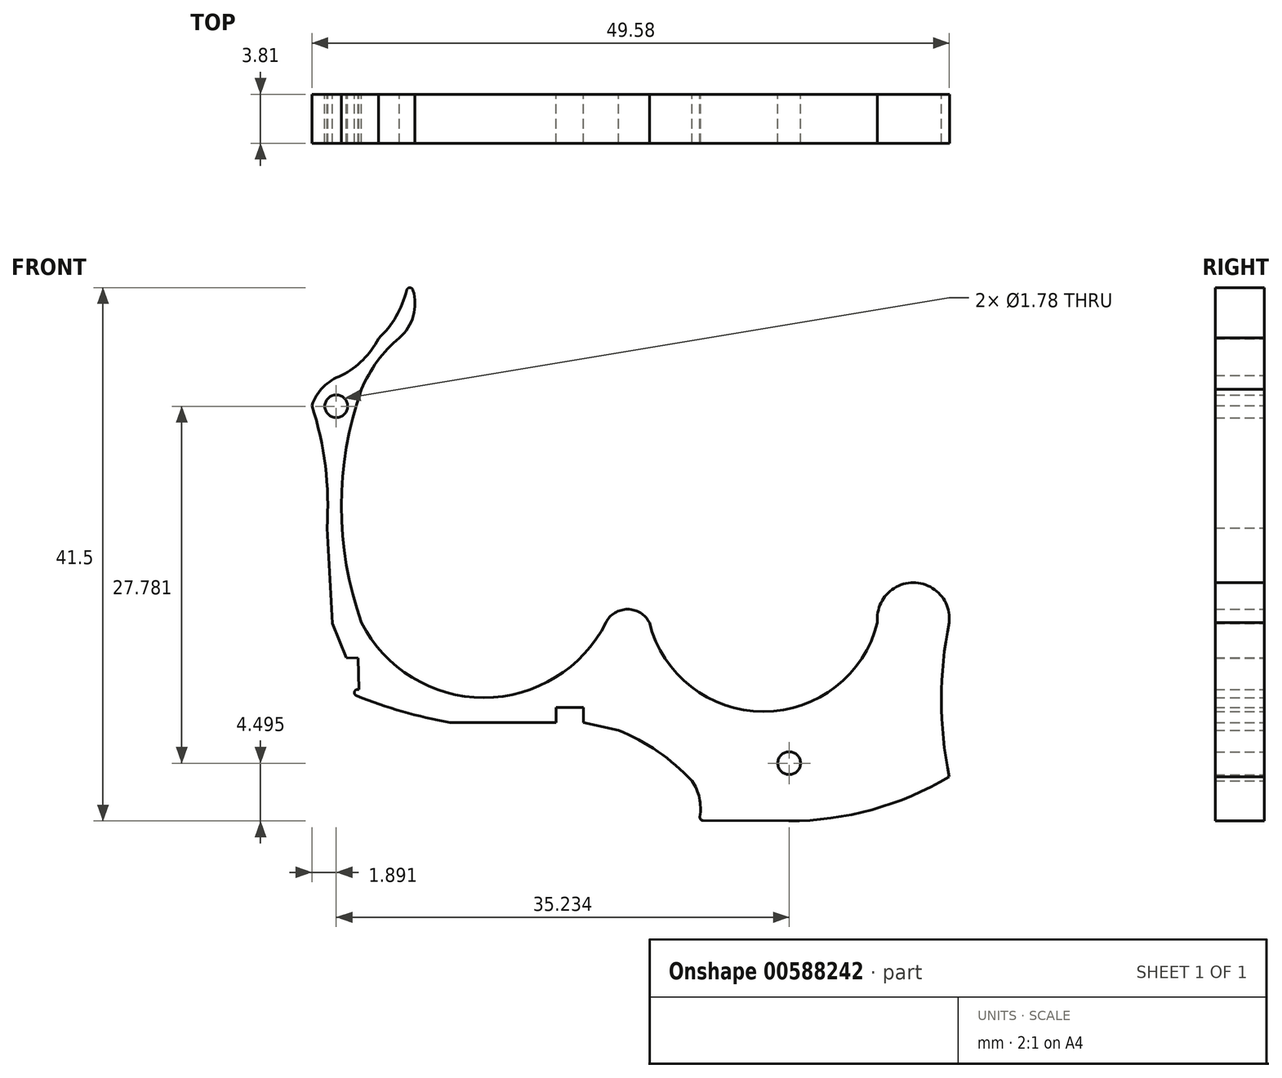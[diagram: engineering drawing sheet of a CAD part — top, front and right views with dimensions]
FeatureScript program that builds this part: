
annotation { "Feature Type Name" : "Feature", "Feature Type Description" : "" }
export const myFeature = defineFeature(function(context is Context, id is Id, definition is map)
    precondition{}
    {
        {
            var Q0;
            Q0=qCreatedBy(makeId("Front.planeOp"),FACE);
            var sketch = newSketch(context, id + "F0", { "sketchPlane" : qUnion([Q0])});
            skArc(sketch, "E0", {"start": v(41.4, 7.53) * mm, "mid": v(38.62, 10.63) * mm, "end": v(35.84, 7.53) * mm});
            skArc(sketch, "E1", {"start": v(-4.3, 25.68) * mm, "mid": v(-5.87, 16.6) * mm, "end": v(-4.3, 7.53) * mm});
            skArc(sketch, "E2", {"start": v(41.4, 7.53) * mm, "mid": v(40.8, 1.52) * mm, "end": v(41.4, -4.48) * mm});
            skArc(sketch, "E3", {"start": v(28.92, -7.91) * mm, "mid": v(35.4, -7.04) * mm, "end": v(41.4, -4.48) * mm});
            skArc(sketch, "E4", {"start": v(-4.3, 7.53) * mm, "mid": v(5.2, 1.69) * mm, "end": v(14.7, 7.53) * mm});
            skArc(sketch, "E5", {"start": v(18.09, 7.53) * mm, "mid": v(26.96, 0.6) * mm, "end": v(35.84, 7.53) * mm});
            skArc(sketch, "E6", {"start": v(14.7, 7.53) * mm, "mid": v(16.4, 8.57) * mm, "end": v(18.09, 7.53) * mm});
            skPoint(sketch, "E7", {"position": v(-22.6, -2.16) * mm});
            skArc(sketch, "E8", {"start": v(-1.35, 29.7) * mm, "mid": v(-3.07, 27.87) * mm, "end": v(-4.3, 25.68) * mm});
            skArc(sketch, "E9", {"start": v(-1.35, 29.7) * mm, "mid": v(-0.18, 31.8) * mm, "end": v(-0.64, 34.17) * mm});
            skPoint(sketch, "E10", {"position": v(-5.35, 30.58) * mm});
            skPoint(sketch, "E11", {"position": v(-9.12, 9) * mm});
            skPoint(sketch, "E12", {"position": v(-32.74, -4.74) * mm});
            skArc(sketch, "E13", {"start": v(-2.97, 29.64) * mm, "mid": v(-1.42, 31.7) * mm, "end": v(-0.64, 34.17) * mm});
            skArc(sketch, "E14", {"start": v(-6.99, 14.9) * mm, "mid": v(-7.11, 19.72) * mm, "end": v(-8.16, 24.43) * mm});
            skArc(sketch, "E15", {"start": v(21.97, -7.88) * mm, "mid": v(22, -6.28) * mm, "end": v(21.4, -4.79) * mm});
            skLineSegment(sketch, "E16", {"start": v(21.97, -7.88) * mm, "end": v(28.92, -7.91) * mm});
            skArc(sketch, "E17", {"start": v(-5.85, 26.76) * mm, "mid": v(-4.2, 27.98) * mm, "end": v(-2.97, 29.64) * mm});
            skArc(sketch, "E18", {"start": v(-5.85, 26.76) * mm, "mid": v(-7.28, 25.86) * mm, "end": v(-8.16, 24.43) * mm});
            skArc(sketch, "E19", {"start": v(-5.73, 2.27) * mm, "mid": v(-1.65, 0.76) * mm, "end": v(2.6, -0.25) * mm});
            skArc(sketch, "E20", {"start": v(21.4, -4.79) * mm, "mid": v(18.75, -2.51) * mm, "end": v(15.68, -0.84) * mm});
            skLineSegment(sketch, "E21", {"start": v(2.6, -0.25) * mm, "end": v(10.83, -0.25) * mm});
            skLineSegment(sketch, "E22", {"start": v(10.83, -0.25) * mm, "end": v(10.83, 0.92) * mm});
            skLineSegment(sketch, "E23", {"start": v(10.83, 0.92) * mm, "end": v(12.97, 0.92) * mm});
            skLineSegment(sketch, "E24", {"start": v(12.97, 0.92) * mm, "end": v(12.97, -0.25) * mm});
            skLineSegment(sketch, "E25", {"start": v(12.97, -0.25) * mm, "end": v(15.68, -0.84) * mm});
            skLineSegment(sketch, "E26", {"start": v(-6.56, 7.46) * mm, "end": v(-6.99, 14.9) * mm});
            skLineSegment(sketch, "E27", {"start": v(-6.56, 7.46) * mm, "end": v(-5.5, 4.8) * mm});
            skLineSegment(sketch, "E28", {"start": v(-5.5, 4.8) * mm, "end": v(-4.56, 4.78) * mm});
            skLineSegment(sketch, "E29", {"start": v(-4.56, 4.78) * mm, "end": v(-4.5, 2.33) * mm});
            skLineSegment(sketch, "E30", {"start": v(-4.5, 2.33) * mm, "end": v(-5.73, 2.27) * mm});
            skPoint(sketch, "E31", {"position": v(28.97, -3.41) * mm});
            skPoint(sketch, "E32", {"position": v(-6.27, 24.37) * mm});
            skSolve(sketch);
        }
        {
            var Q0;
            Q0=makeQuery(id+"F0.imprint","IMPRINT",FACE,{"disambiguationData":[TD([[makeQuery(id+"F0.imprint","IMPRINT",EDGE,{"derivedFrom":sQuery(id+"F0.wireOp",EDGE,"AFGxsh7R-k0zL-6gKK-qfLR-BOf17Wv1HaxV")}),-1.0]])]});
            var Q1;
            Q1=makeQuery(id+"F0.imprint","IMPRINT",FACE,{"disambiguationData":[TD([[makeQuery(id+"F0.imprint","IMPRINT",EDGE,{"derivedFrom":sQuery(id+"F0.wireOp",EDGE,"E0")}),1.0]])]});
            extrude(context, id + "F1", {"entities" : qUnion([Q0, Q1]), "depth" : 3.8 * mm, "offsetDistance" : 25.4 * mm});
        }
        {
            var Q0;
            Q0=makeQuery(id+"F1.opExtrude","SWEPT_EDGE",EDGE,{"disambiguationData":[OSD([sQuery(id+"F0.wireOp",EDGE,"E9"),sQuery(id+"F0.wireOp",EDGE,"E13")])]});
            var Q1;
            Q1=makeQuery(id+"F1.opExtrude","SWEPT_EDGE",EDGE,{"disambiguationData":[OSD([sQuery(id+"F0.wireOp",EDGE,"E15"),sQuery(id+"F0.wireOp",EDGE,"E16")])]});
            var Q2;
            Q2=makeQuery(id+"F1.opExtrude","SWEPT_EDGE",EDGE,{"disambiguationData":[OSD([sQuery(id+"F0.wireOp",EDGE,"PraF7M6a-4R2M-S6ax-mL7v-wy4y3stJjaV9"),sQuery(id+"F0.wireOp",EDGE,"E19")])]});
            fillet(context, id + "F2", {"entities" : qUnion([Q0, Q1, Q2]), "radius" : 0.25 * mm, "tangentPropagation" : true, "allowEdgeOverflow" : false});
        }
        {
            var Q0;
            Q0=sQuery(id+"F0.wireOp",VERTEX,"E31");
            var Q1;
            Q1=sQuery(id+"F0.wireOp",VERTEX,"E32");
            var Q2;
            Q2=makeQuery(id+"F1.opExtrude","SWEPT_BODY",BODY,{"disambiguationData":[OSD([sQuery(id+"F0.wireOp",EDGE,"E0"),sQuery(id+"F0.wireOp",EDGE,"E1"),sQuery(id+"F0.wireOp",EDGE,"E2"),sQuery(id+"F0.wireOp",EDGE,"E3"),sQuery(id+"F0.wireOp",EDGE,"E4"),sQuery(id+"F0.wireOp",EDGE,"E5"),sQuery(id+"F0.wireOp",EDGE,"E6"),sQuery(id+"F0.wireOp",EDGE,"E8"),sQuery(id+"F0.wireOp",EDGE,"E9"),sQuery(id+"F0.wireOp",EDGE,"E13"),sQuery(id+"F0.wireOp",EDGE,"E14"),sQuery(id+"F0.wireOp",EDGE,"E15"),sQuery(id+"F0.wireOp",EDGE,"E16"),sQuery(id+"F0.wireOp",EDGE,"E17"),sQuery(id+"F0.wireOp",EDGE,"E18"),sQuery(id+"F0.wireOp",EDGE,"E19"),sQuery(id+"F0.wireOp",EDGE,"E20"),sQuery(id+"F0.wireOp",EDGE,"E21"),sQuery(id+"F0.wireOp",EDGE,"E22"),sQuery(id+"F0.wireOp",EDGE,"E23"),sQuery(id+"F0.wireOp",EDGE,"E24"),sQuery(id+"F0.wireOp",EDGE,"E25"),sQuery(id+"F0.wireOp",EDGE,"E26"),sQuery(id+"F0.wireOp",EDGE,"E27"),sQuery(id+"F0.wireOp",EDGE,"E28"),sQuery(id+"F0.wireOp",EDGE,"E29"),sQuery(id+"F0.wireOp",EDGE,"E30")])]});
            hole(context, id + "F3", {"style" : HoleStyle.SIMPLE, "endStyle" : HoleEndStyle.THROUGH, "oppositeDirection" : true, "holeDiameter" : 1.78 * mm, "majorDiameter" : 6.35 * mm, "isTappedThrough" : true, "tappedDepth" : 12.7 * mm, "tapClearance" : 3, "locations" : qUnion([Q0, Q1]), "scope" : qUnion([Q2])});
        }
    });
